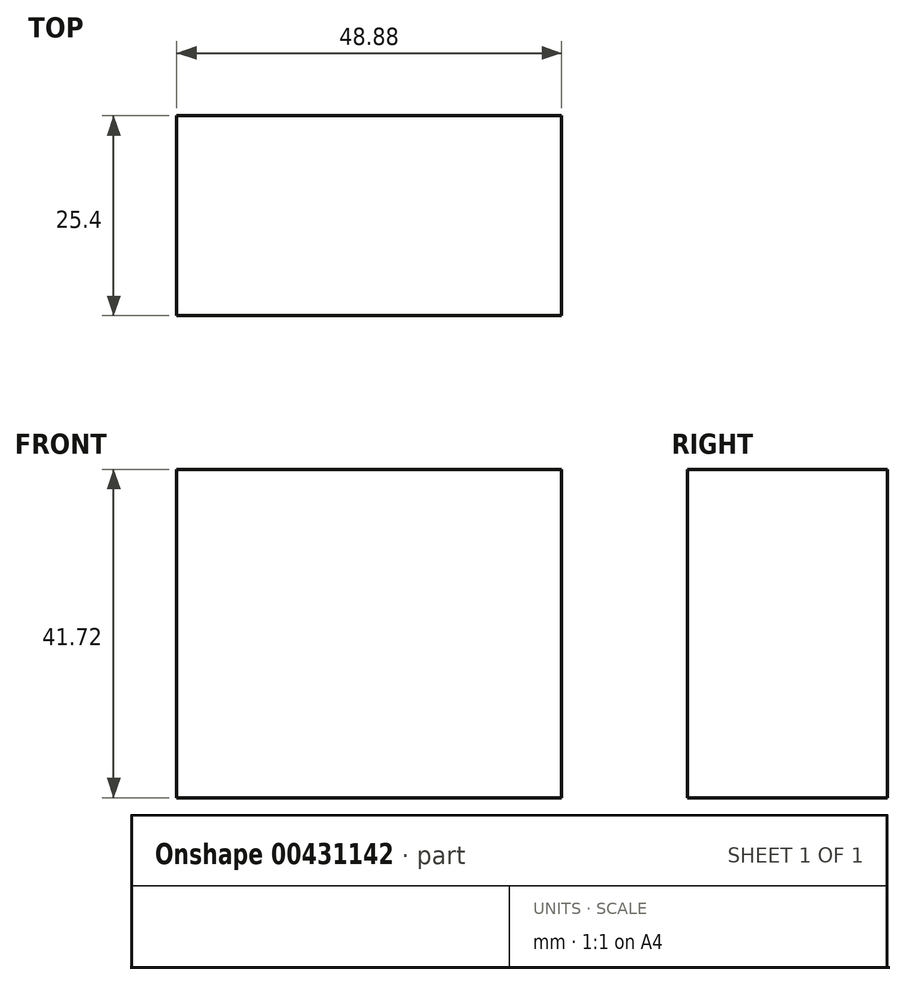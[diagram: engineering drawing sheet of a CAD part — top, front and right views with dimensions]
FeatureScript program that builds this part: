
annotation { "Feature Type Name" : "Feature", "Feature Type Description" : "" }
export const myFeature = defineFeature(function(context is Context, id is Id, definition is map)
    precondition{}
    {
        {
            var Q0;
            Q0=qCreatedBy(makeId("Front.planeOp"),FACE);
            var sketch = newSketch(context, id + "F0", { "sketchPlane" : qUnion([Q0])});
            skLineSegment(sketch, "E0.bottom", {"start": v(24.44, -20.86) * mm, "end": v(-24.44, -20.86) * mm});
            skLineSegment(sketch, "E0.top", {"start": v(24.44, 20.86) * mm, "end": v(-24.44, 20.86) * mm});
            skLineSegment(sketch, "E0.left", {"start": v(24.44, -20.86) * mm, "end": v(24.44, 20.86) * mm});
            skLineSegment(sketch, "E0.right", {"start": v(-24.44, -20.86) * mm, "end": v(-24.44, 20.86) * mm});
            skPoint(sketch, "E0.middle", {"position": v(0, 0) * mm});
            skSolve(sketch);
        }
        {
            var Q0;
            Q0=makeQuery(id+"F0.imprint","IMPRINT",FACE,{"disambiguationData":[TD([[makeQuery(id+"F0.imprint","IMPRINT",EDGE,{"derivedFrom":sQuery(id+"F0.wireOp",EDGE,"E0.bottom")}),-1.0]])]});
            extrude(context, id + "F1", {"entities" : qUnion([Q0]), "depth" : 25.4 * mm});
        }
    });
